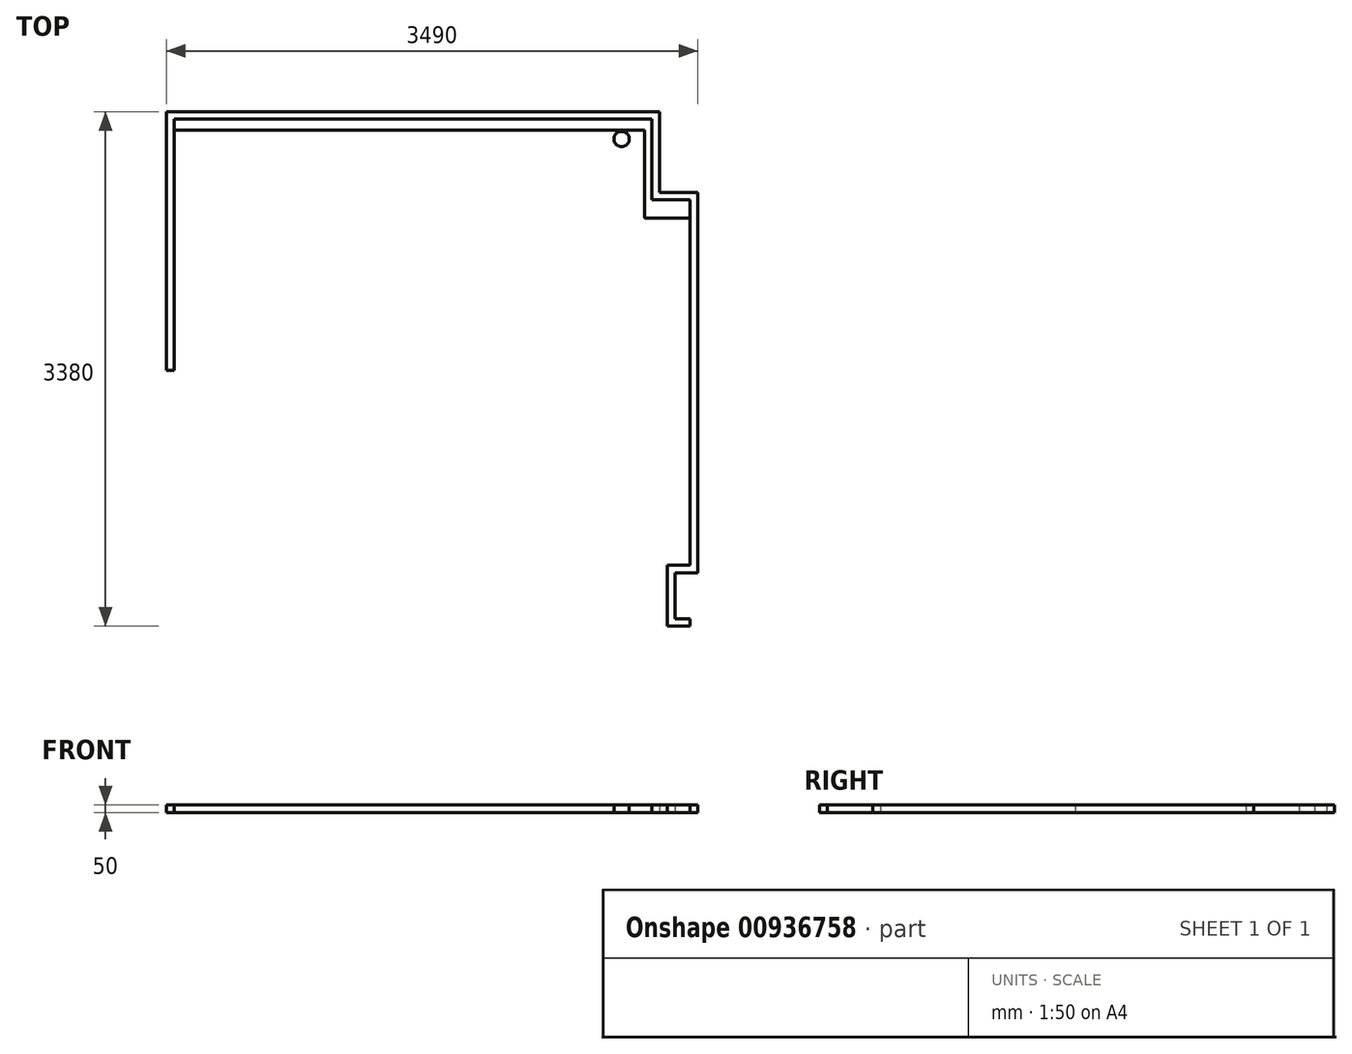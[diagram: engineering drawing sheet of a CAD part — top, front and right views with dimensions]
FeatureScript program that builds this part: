
annotation { "Feature Type Name" : "Feature", "Feature Type Description" : "" }
export const myFeature = defineFeature(function(context is Context, id is Id, definition is map)
    precondition{}
    {
        {
            var Q0;
            Q0=qCreatedBy(makeId("Top.planeOp"),FACE);
            var sketch = newSketch(context, id + "F0", { "sketchPlane" : qUnion([Q0])});
            skLineSegment(sketch, "E0", {"start": v(-250, 0) * mm, "end": v(0, 0) * mm, "construction": true});
            skLineSegment(sketch, "E1", {"start": v(0, 0) * mm, "end": v(0, -530) * mm, "construction": true});
            skCircle(sketch, "E2", {"center": v(-450, -130) * mm, "radius": 50 * mm});
            skLineSegment(sketch, "E3", {"start": v(-250, 0) * mm, "end": v(-250, -530) * mm});
            skLineSegment(sketch, "E4", {"start": v(-250, -530) * mm, "end": v(0, -530) * mm});
            skLineSegment(sketch, "E5", {"start": v(-250, 0) * mm, "end": v(-3390, 0) * mm});
            skLineSegment(sketch, "E6", {"start": v(0, -530) * mm, "end": v(0, -2930) * mm});
            skLineSegment(sketch, "E7", {"start": v(-3390, 0) * mm, "end": v(-3390, -1650) * mm});
            skLineSegment(sketch, "E8", {"start": v(0, -2930) * mm, "end": v(-150, -2930) * mm});
            skLineSegment(sketch, "E9", {"start": v(-150, -2930) * mm, "end": v(-150, -3330) * mm});
            skLineSegment(sketch, "E10", {"start": v(-150, -3330) * mm, "end": v(0, -3330) * mm});
            skLineSegment(sketch, "E11", {"start": v(-3390, -70) * mm, "end": v(-250, -70) * mm, "construction": true});
            skLineSegment(sketch, "E12", {"start": v(-300, -70) * mm, "end": v(-300, -650) * mm, "construction": true});
            skLineSegment(sketch, "E13", {"start": v(-300, -650) * mm, "end": v(0, -650) * mm, "construction": true});
            skSolve(sketch);
        }
        {
            var Q0;
            Q0=qCreatedBy(makeId("Top.planeOp"),FACE);
            var sketch = newSketch(context, id + "F1", { "sketchPlane" : qUnion([Q0])});
            skLineSegment(sketch, "E14.0", {"start": v(-3390, 0) * mm, "end": v(-3390, -1650) * mm});
            skLineSegment(sketch, "E14.1", {"start": v(-250, 0) * mm, "end": v(-3390, 0) * mm});
            skLineSegment(sketch, "E14.2", {"start": v(-250, 0) * mm, "end": v(-250, -530) * mm});
            skLineSegment(sketch, "E14.3", {"start": v(-250, -530) * mm, "end": v(0, -530) * mm});
            skLineSegment(sketch, "E14.4", {"start": v(0, -530) * mm, "end": v(0, -2930) * mm});
            skLineSegment(sketch, "E14.5", {"start": v(0, -2930) * mm, "end": v(-150, -2930) * mm});
            skLineSegment(sketch, "E14.6", {"start": v(-150, -2930) * mm, "end": v(-150, -3330) * mm});
            skLineSegment(sketch, "E14.7", {"start": v(-150, -3330) * mm, "end": v(0, -3330) * mm});
            skLineSegment(sketch, "E15.0", {"start": v(-3440, 50) * mm, "end": v(-3440, -1650) * mm});
            skLineSegment(sketch, "E15.1", {"start": v(-200, 50) * mm, "end": v(-3440, 50) * mm});
            skLineSegment(sketch, "E15.2", {"start": v(-200, 50) * mm, "end": v(-200, -480) * mm});
            skLineSegment(sketch, "E15.3", {"start": v(-200, -480) * mm, "end": v(50, -480) * mm});
            skLineSegment(sketch, "E15.4", {"start": v(-100, -3280) * mm, "end": v(0, -3280) * mm});
            skLineSegment(sketch, "E15.5", {"start": v(-100, -2980) * mm, "end": v(-100, -3280) * mm});
            skLineSegment(sketch, "E15.6", {"start": v(50, -2980) * mm, "end": v(-100, -2980) * mm});
            skLineSegment(sketch, "E15.7", {"start": v(50, -480) * mm, "end": v(50, -2980) * mm});
            skLineSegment(sketch, "E16", {"start": v(-3390, -1650) * mm, "end": v(-3440, -1650) * mm});
            skLineSegment(sketch, "E17", {"start": v(0, -3330) * mm, "end": v(0, -3280) * mm});
            skCircle(sketch, "E18.0", {"center": v(-450, -130) * mm, "radius": 50 * mm});
            skSolve(sketch);
        }
        {
            var Q0;
            Q0 = qSketchRegion(id + "F1", true);
            extrude(context, id + "F2", {"entities" : qUnion([Q0]), "depth" : 50 * mm, "offsetDistance" : 25 * mm});
        }
        {
            var Q0;
            Q0=qCreatedBy(makeId("Top.planeOp"),FACE);
            var sketch = newSketch(context, id + "F3", { "sketchPlane" : qUnion([Q0])});
            skLineSegment(sketch, "E19.0", {"start": v(-3390, -70) * mm, "end": v(-300, -70) * mm});
            skLineSegment(sketch, "E19.1", {"start": v(-250, 0) * mm, "end": v(-3390, 0) * mm});
            skLineSegment(sketch, "E19.2", {"start": v(-3390, 0) * mm, "end": v(-3390, -70) * mm});
            skLineSegment(sketch, "E19.3", {"start": v(-300, -70) * mm, "end": v(-300, -650) * mm});
            skLineSegment(sketch, "E19.4", {"start": v(-250, 0) * mm, "end": v(-250, -530) * mm});
            skLineSegment(sketch, "E19.5", {"start": v(-300, -650) * mm, "end": v(0, -650) * mm});
            skLineSegment(sketch, "E19.6", {"start": v(-250, -530) * mm, "end": v(0, -530) * mm});
            skLineSegment(sketch, "E19.7", {"start": v(0, -530) * mm, "end": v(0, -650) * mm});
            skPoint(sketch, "E20.orphan", {"position": v(-250, -70) * mm});
            skPoint(sketch, "E21.orphan", {"position": v(0, -2930) * mm});
            skPoint(sketch, "E22.orphan", {"position": v(-3390, -1650) * mm});
            skSolve(sketch);
        }
        {
            var Q0;
            Q0 = qSketchRegion(id + "F3", true);
            extrude(context, id + "F4", {"entities" : qUnion([Q0]), "depth" : 1 * mm, "offsetDistance" : 25 * mm});
        }
    });
